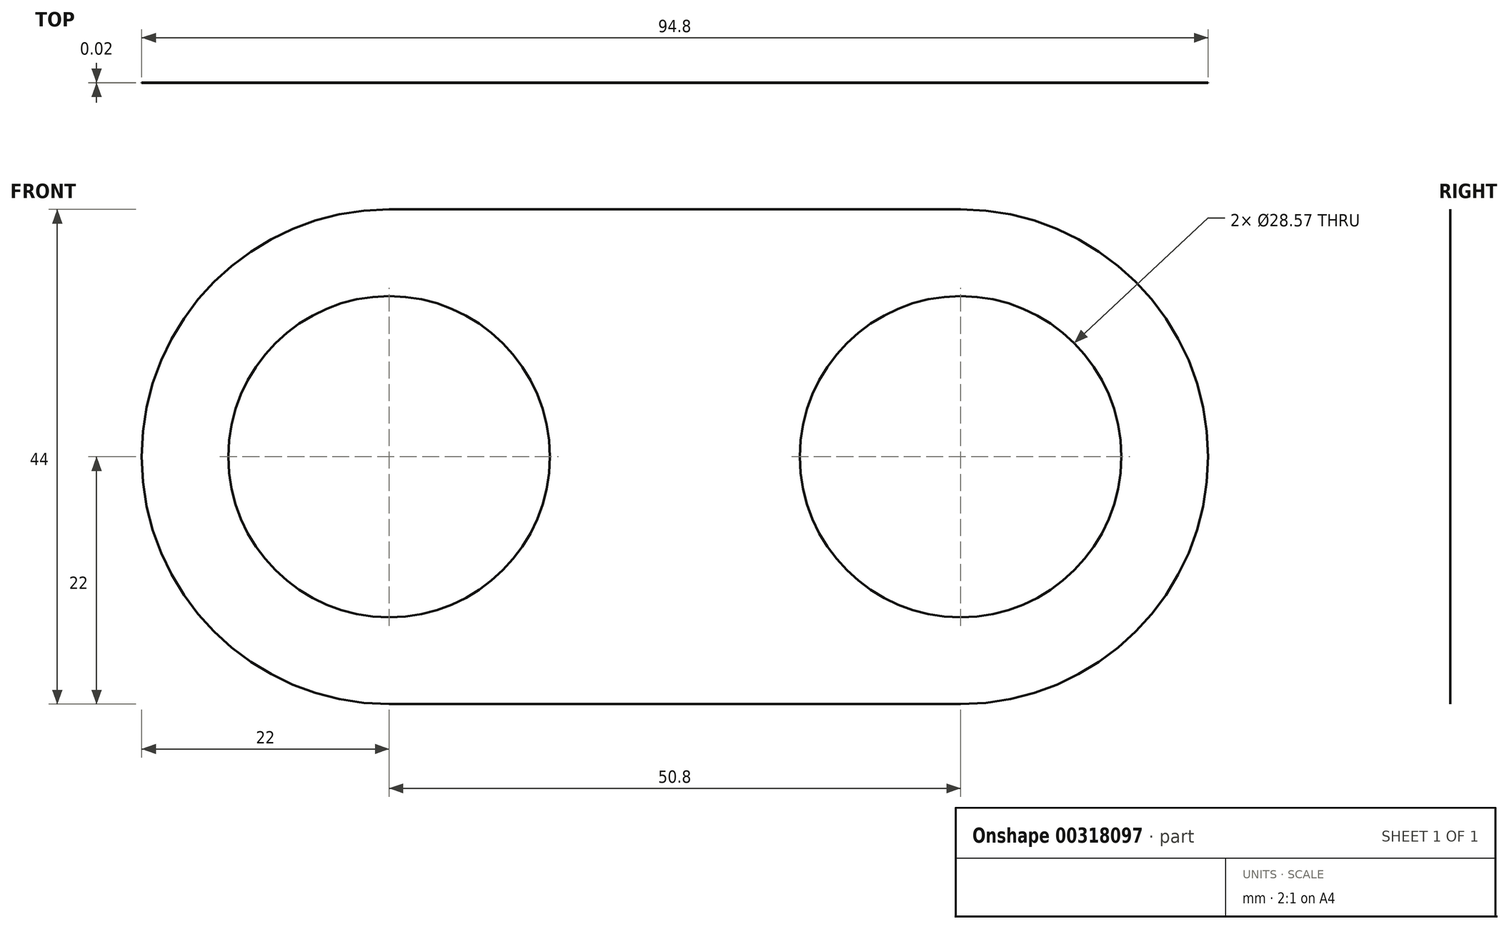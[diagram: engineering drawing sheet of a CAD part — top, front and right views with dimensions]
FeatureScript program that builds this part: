
annotation { "Feature Type Name" : "Feature", "Feature Type Description" : "" }
export const myFeature = defineFeature(function(context is Context, id is Id, definition is map)
    precondition{}
    {
        {
            var Q0;
            Q0=qCreatedBy(makeId("Front.planeOp"),FACE);
            var sketch = newSketch(context, id + "F0", { "sketchPlane" : qUnion([Q0])});
            skLineSegment(sketch, "E0.bottom", {"start": v(25.4, 0) * mm, "end": v(-25.4, 0) * mm, "construction": true});
            skPoint(sketch, "E0.middle", {"position": v(0, 0) * mm});
            skCircle(sketch, "E1", {"center": v(-25.4, 0) * mm, "radius": 14.29 * mm});
            skCircle(sketch, "E2", {"center": v(25.4, 0) * mm, "radius": 14.29 * mm});
            skLineSegment(sketch, "E3.bottom", {"start": v(-25.4, 22) * mm, "end": v(25.4, 22) * mm});
            skPoint(sketch, "E4.orphan", {"position": v(-47.4, 22) * mm});
            skPoint(sketch, "E5.orphan", {"position": v(47.4, 22) * mm});
            skArc(sketch, "E6", {"start": v(-25.4, 22) * mm, "mid": v(-40.96, 15.56) * mm, "end": v(-47.4, 0) * mm});
            skArc(sketch, "E7", {"start": v(47.4, 0) * mm, "mid": v(40.96, 15.56) * mm, "end": v(25.4, 22) * mm});
            skArc(sketch, "E8.MirrorCS", {"start": v(47.4, 0) * mm, "mid": v(40.96, -15.56) * mm, "end": v(25.4, -22) * mm});
            skArc(sketch, "E9.MirrorCS", {"start": v(-25.4, -22) * mm, "mid": v(-40.96, -15.56) * mm, "end": v(-47.4, 0) * mm});
            skLineSegment(sketch, "E10.MirrorCS", {"start": v(-25.4, -22) * mm, "end": v(25.4, -22) * mm});
            skPoint(sketch, "E11.MirrorP", {"position": v(-47.4, -22) * mm});
            skPoint(sketch, "E12.MirrorP", {"position": v(47.4, -22) * mm});
            skSolve(sketch);
        }
        {
            var Q0;
            Q0=qSketchRegion(id+"F0",true);
            var Q1;
            Q1=makeQuery(id+"F0.imprint","IMPRINT",FACE,{"disambiguationData":[TD([[makeQuery(id+"F0.imprint","IMPRINT",EDGE,{"derivedFrom":sQuery(id+"F0.wireOp",EDGE,"E1")}),-1.0]])]});
            var Q2;
            Q2=makeQuery(id+"F0.imprint","IMPRINT",FACE,{"disambiguationData":[TD([[makeQuery(id+"F0.imprint","IMPRINT",EDGE,{"derivedFrom":sQuery(id+"F0.wireOp",EDGE,"E2")}),-1.0]])]});
            var Q3;
            Q3=makeQuery(id+"F0.imprint","IMPRINT",FACE,{"disambiguationData":[TD([[makeQuery(id+"F0.imprint","IMPRINT",EDGE,{"derivedFrom":sQuery(id+"F0.wireOp",EDGE,"a93d44b6-50e8-4925-9ba8-c7bf3ba64ab15.MirrorC")}),-1.0]])]});
            var Q4;
            Q4=makeQuery(id+"F0.imprint","IMPRINT",FACE,{"disambiguationData":[TD([[makeQuery(id+"F0.imprint","IMPRINT",EDGE,{"derivedFrom":sQuery(id+"F0.wireOp",EDGE,"a93d44b6-50e8-4925-9ba8-c7bf3ba64ab14.MirrorC")}),-1.0]])]});
            extrude(context, id + "F1", {"entities" : qUnion([Q0, Q1, Q2, Q3, Q4]), "depth" : 5 / 203.2 * mm, "offsetDistance" : 25.4 * mm});
        }
    });
